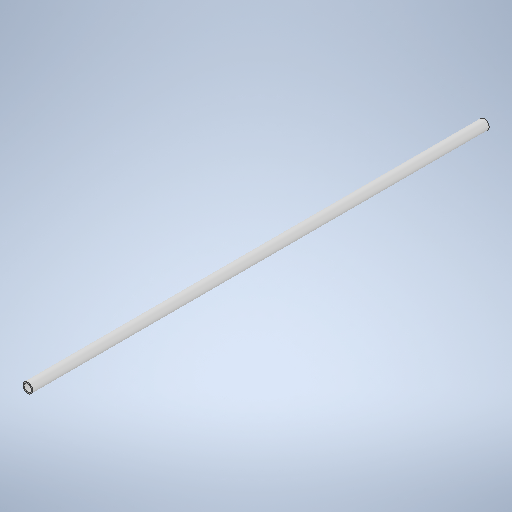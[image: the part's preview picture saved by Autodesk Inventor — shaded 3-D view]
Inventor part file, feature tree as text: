
AUTODESK INVENTOR PART (.ipt)
format: ipt  version: 2025 (Build 290162000, 162)  size: 249,856 bytes
history: native  units: in
note: dims shown in document units (in); Inventor stores cm internally (conversion verified against a paired STEP export)
features: extrude x1, sketch x1
ambient origin geometry x8: Origin, YZ Plane, XZ Plane, XY Plane, X Axis, Y Axis, Z Axis, Center Point
bodies: Solid1 (feature_tree)
feature tree (2):
  extrude  "Extrusion1"  Depth=48.0in
  sketch  "Sketch1"  dims[d0=1.04in d1=0.8in d2=48.0in d3=0.0in]
